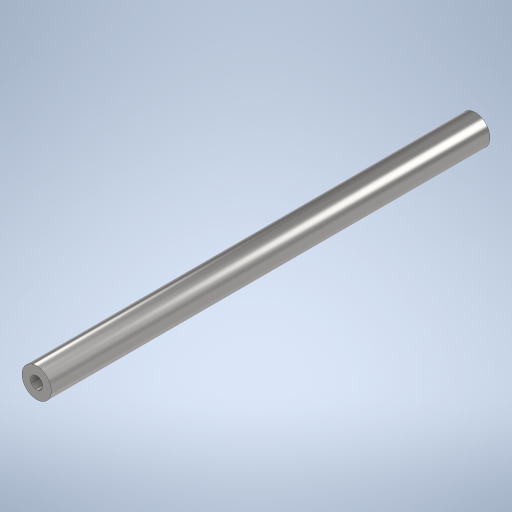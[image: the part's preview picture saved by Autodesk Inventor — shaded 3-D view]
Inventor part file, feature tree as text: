
AUTODESK INVENTOR PART (.ipt)
format: ipt  version: 2023 (Build 270158000, 158)  size: 276,992 bytes
history: native  units: mm
features: extrude x3, sketch x3
ambient origin geometry x8: Origin, YZ Plane, XZ Plane, XY Plane, X Axis, Y Axis, Z Axis, Center Point
bodies: Solid1 (feature_tree)
feature tree (6):
  extrude  "Extrusion1"  Depth=75.0mm TaperAngle=0.0deg
  extrude  "Extrusion2"  Depth=20.0mm TaperAngle=0.0deg
  extrude  "Extrusion3"  [1 undecoded]
  sketch  "Sketch1"  dims[d0=5.0mm d1=75.0mm d2=0.0mm]
  sketch  "Sketch2"  dims[d3=2.05mm d4=20.0mm d5=0.0mm]
  sketch  "Sketch3"  dims[d6=20.0mm d7=0.0mm]
note: 1 required parameter value undecoded (feature->parameter linkage not recoverable at this tier; creation-order binding heuristic only, values carry confidence <= 0.55)
